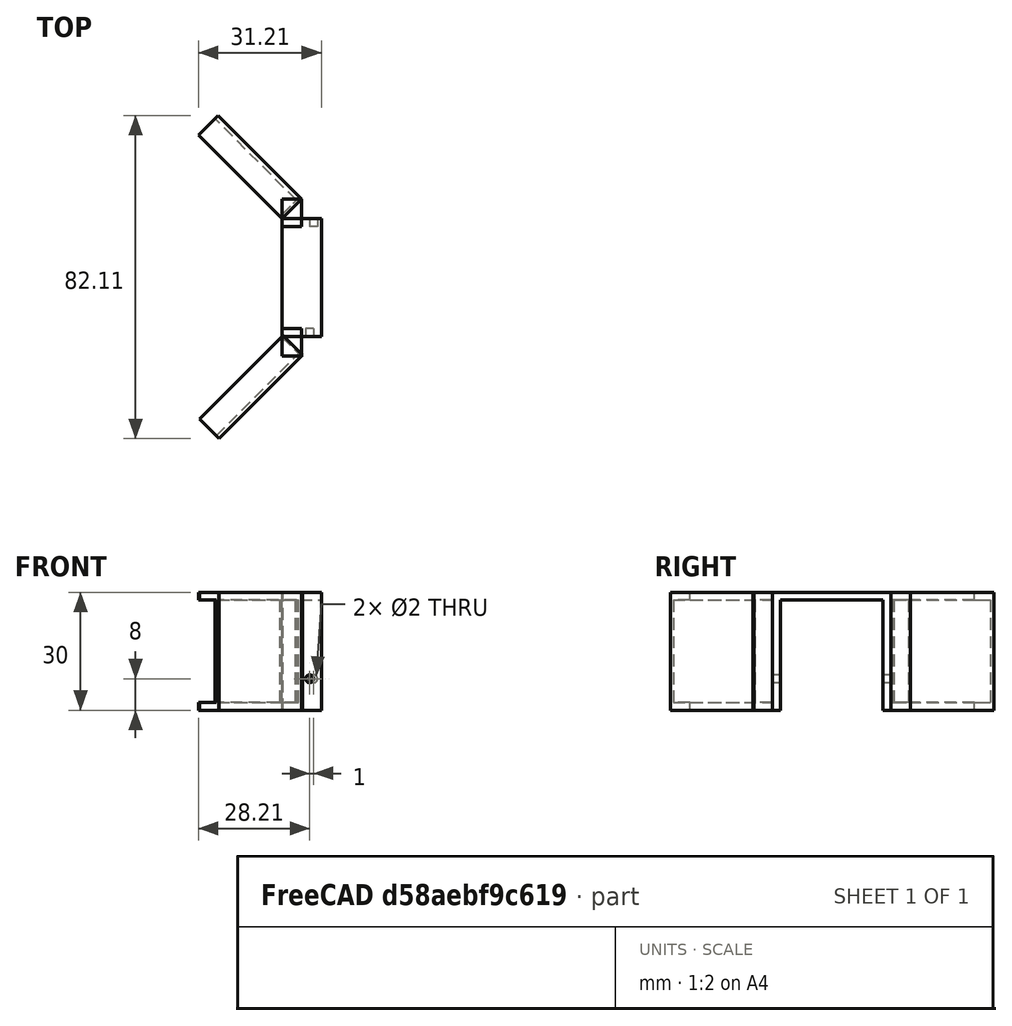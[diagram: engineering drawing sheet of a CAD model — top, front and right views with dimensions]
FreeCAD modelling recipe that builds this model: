
FCSTD DOCUMENT  (FreeCAD 0.17R13522 (Git))
Label: doublemirrorholder
License: All rights reserved
LicenseURL: http://en.wikipedia.org/wiki/All_rights_reserved
objects: Part::Box×8, Part::Cut×7, Part::Cylinder×2
note: 17 computed .brp shape members not serialized (recipe doc carries the construction recipe); baked Part::Feature solids carry a one-line shape summary decoded from their .brp

FEATURE [Part::Box] Box  label="Cube"
  AttacherType = Attacher::AttachEngine3D
  Height = 30
  Length = 10
  Width = 30
FEATURE [Part::Box] Box001  label="Cube001"
  AttacherType = Attacher::AttachEngine3D
  Height = 29
  Length = 45
  Placement = pos=(-6,2,-1) rot=(0,0,1;0rad)
  Width = 26
FEATURE [Part::Box] Box002  label="Cube002"
  AttacherType = Attacher::AttachEngine3D
  Height = 30
  Length = 7
  Placement = pos=(0,30,0) rot=(0,0,1;0.785398rad)
  Width = 30
FEATURE [Part::Box] Box003  label="Cube003"
  AttacherType = Attacher::AttachEngine3D
  Height = 30
  Length = 7
  Placement = pos=(-21,-21,0) rot=(0,0,-1;0.785398rad)
  Width = 30
FEATURE [Part::Cut] Cut
  Base = -> Box
  Tool = -> Box001
FEATURE [Part::Cylinder] Cylinder
  Angle = 360
  AttacherType = Attacher::AttachEngine3D
  Height = 10
  Placement = pos=(8,35,8) rot=(1,0,0;1.5708rad)
  Radius = 1
FEATURE [Part::Cylinder] Cylinder001
  Angle = 360
  AttacherType = Attacher::AttachEngine3D
  Height = 10
  Placement = pos=(7,6,8) rot=(1,0,0;1.5708rad)
  Radius = 1
FEATURE [Part::Cut] Cut001
  Base = -> Cut
  Tool = -> Cylinder001
FEATURE [Part::Cut] Cut002
  Base = -> Cut001
  Tool = -> Cylinder
FEATURE [Part::Box] Box004  label="Cube004"
  AttacherType = Attacher::AttachEngine3D
  Height = 26
  Length = 8
  Placement = pos=(-2,29,2) rot=(0,0,1;0.785398rad)
  Width = 34
FEATURE [Part::Box] Box005  label="Cube005"
  AttacherType = Attacher::AttachEngine3D
  Height = 26
  Length = 6
  Placement = pos=(-22,-22,2) rot=(0,0,-1;0.785398rad)
  Width = 31
FEATURE [Part::Cut] Cut003
  Base = -> Box003
  Tool = -> Box005
FEATURE [Part::Cut] Cut004
  Base = -> Box002
  Tool = -> Box004
FEATURE [Part::Box] Box006  label="Cube006"
  AttacherType = Attacher::AttachEngine3D
  Height = 30
  Length = 5
  Placement = pos=(0,-5,0) rot=(0,0,1;0rad)
  Width = 7
FEATURE [Part::Box] Box007  label="Cube007"
  AttacherType = Attacher::AttachEngine3D
  Height = 30
  Length = 5
  Placement = pos=(0,28,0) rot=(0,0,1;0rad)
  Width = 7
FEATURE [Part::Cut] Cut005
  Base = -> Box007
  Tool = -> Box004
FEATURE [Part::Cut] Cut006
  Base = -> Box006
  Tool = -> Box005
